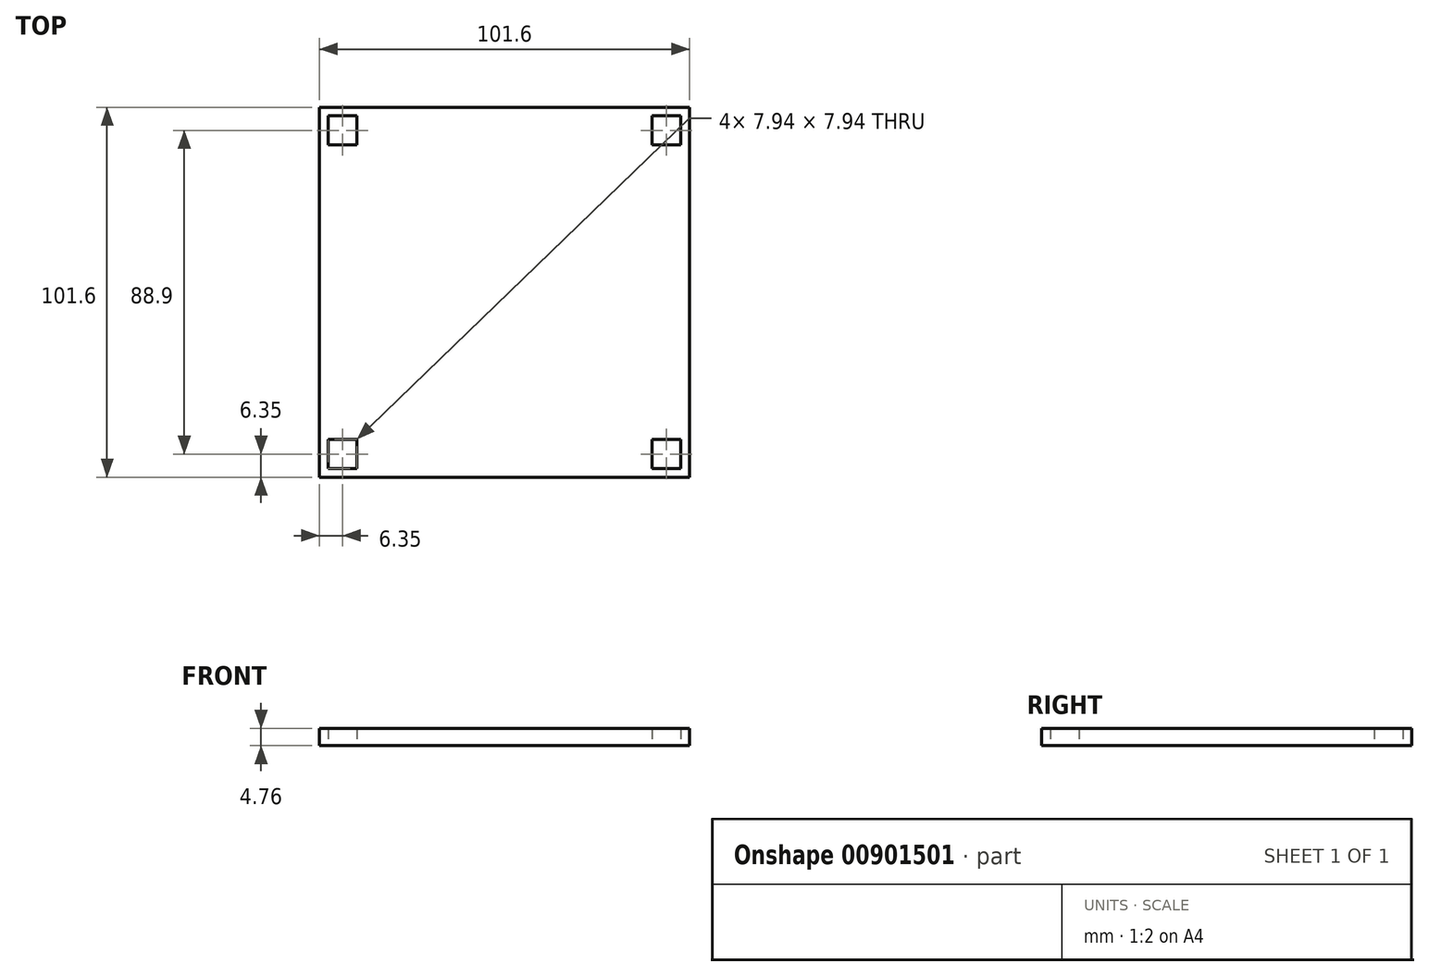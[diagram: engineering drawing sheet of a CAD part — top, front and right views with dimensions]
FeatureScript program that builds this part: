
annotation { "Feature Type Name" : "Feature", "Feature Type Description" : "" }
export const myFeature = defineFeature(function(context is Context, id is Id, definition is map)
    precondition{}
    {
        {
            var Q0;
            Q0=qCreatedBy(makeId("Top.planeOp"),FACE);
            var sketch = newSketch(context, id + "F0", { "sketchPlane" : qUnion([Q0])});
            skLineSegment(sketch, "E0.bottom", {"start": v(0, 0) * mm, "end": v(101.6, 0) * mm});
            skLineSegment(sketch, "E0.top", {"start": v(0, 101.6) * mm, "end": v(101.6, 101.6) * mm});
            skLineSegment(sketch, "E0.left", {"start": v(0, 0) * mm, "end": v(0, 101.6) * mm});
            skLineSegment(sketch, "E0.right", {"start": v(101.6, 0) * mm, "end": v(101.6, 101.6) * mm});
            skLineSegment(sketch, "E1.bottom", {"start": v(19.05, 12.7) * mm, "end": v(82.55, 12.7) * mm, "construction": true});
            skLineSegment(sketch, "E1.top", {"start": v(19.05, 88.9) * mm, "end": v(82.55, 88.9) * mm, "construction": true});
            skLineSegment(sketch, "E1.left", {"start": v(12.7, 19.05) * mm, "end": v(12.7, 82.55) * mm, "construction": true});
            skLineSegment(sketch, "E1.right", {"start": v(88.9, 19.05) * mm, "end": v(88.9, 82.55) * mm, "construction": true});
            skPoint(sketch, "E2.visualSharp", {"position": v(12.7, 12.7) * mm});
            skArc(sketch, "E2.filletArc", {"start": v(12.7, 19.05) * mm, "mid": v(14.56, 14.56) * mm, "end": v(19.05, 12.7) * mm, "construction": true});
            skPoint(sketch, "E3.visualSharp", {"position": v(88.9, 12.7) * mm});
            skArc(sketch, "E3.filletArc", {"start": v(82.55, 12.7) * mm, "mid": v(87.04, 14.56) * mm, "end": v(88.9, 19.05) * mm, "construction": true});
            skPoint(sketch, "E4.visualSharp", {"position": v(88.9, 88.9) * mm});
            skArc(sketch, "E4.filletArc", {"start": v(88.9, 82.55) * mm, "mid": v(87.04, 87.04) * mm, "end": v(82.55, 88.9) * mm, "construction": true});
            skPoint(sketch, "E5.visualSharp", {"position": v(12.7, 88.9) * mm});
            skArc(sketch, "E5.filletArc", {"start": v(19.05, 88.9) * mm, "mid": v(14.56, 87.04) * mm, "end": v(12.7, 82.55) * mm, "construction": true});
            skLineSegment(sketch, "E6", {"start": v(88.9, 12.7) * mm, "end": v(101.6, 0) * mm, "construction": true});
            skLineSegment(sketch, "E7", {"start": v(12.7, 12.7) * mm, "end": v(0, 0) * mm, "construction": true});
            skLineSegment(sketch, "E8", {"start": v(6.35, 6.35) * mm, "end": v(95.25, 6.35) * mm, "construction": true});
            skLineSegment(sketch, "E9", {"start": v(0, 101.6) * mm, "end": v(12.7, 88.9) * mm, "construction": true});
            skLineSegment(sketch, "E10", {"start": v(88.9, 88.9) * mm, "end": v(101.6, 101.6) * mm, "construction": true});
            skLineSegment(sketch, "E11", {"start": v(95.25, 95.25) * mm, "end": v(6.35, 95.25) * mm, "construction": true});
            skLineSegment(sketch, "E12", {"start": v(6.35, 95.25) * mm, "end": v(6.35, 6.35) * mm, "construction": true});
            skLineSegment(sketch, "E13", {"start": v(95.25, 6.35) * mm, "end": v(95.25, 95.25) * mm, "construction": true});
            skCircle(sketch, "E14", {"center": v(6.35, 95.25) * mm, "radius": 3.97 * mm, "construction": true});
            skCircle(sketch, "E15.0.1.0", {"center": v(6.35, 6.35) * mm, "radius": 3.97 * mm, "construction": true});
            skCircle(sketch, "E15.1.0.0", {"center": v(95.25, 95.25) * mm, "radius": 3.97 * mm, "construction": true});
            skCircle(sketch, "E15.1.1.0", {"center": v(95.25, 6.35) * mm, "radius": 3.97 * mm, "construction": true});
            skLineSegment(sketch, "E15.direction1", {"start": v(6.35, 95.25) * mm, "end": v(95.25, 95.25) * mm, "construction": true});
            skLineSegment(sketch, "E16.bottom", {"start": v(2.38, 2.38) * mm, "end": v(10.32, 2.38) * mm});
            skLineSegment(sketch, "E16.top", {"start": v(2.38, 10.32) * mm, "end": v(10.32, 10.32) * mm});
            skLineSegment(sketch, "E16.left", {"start": v(2.38, 2.38) * mm, "end": v(2.38, 10.32) * mm});
            skLineSegment(sketch, "E16.right", {"start": v(10.32, 2.38) * mm, "end": v(10.32, 10.32) * mm});
            skLineSegment(sketch, "E17.0.1.0", {"start": v(10.32, 91.28) * mm, "end": v(10.32, 99.22) * mm});
            skLineSegment(sketch, "E17.0.1.1", {"start": v(2.38, 99.22) * mm, "end": v(10.32, 99.22) * mm});
            skLineSegment(sketch, "E17.0.1.2", {"start": v(2.38, 91.28) * mm, "end": v(2.38, 99.22) * mm});
            skLineSegment(sketch, "E17.0.1.3", {"start": v(2.38, 91.28) * mm, "end": v(10.32, 91.28) * mm});
            skLineSegment(sketch, "E17.1.0.0", {"start": v(99.22, 2.38) * mm, "end": v(99.22, 10.32) * mm});
            skLineSegment(sketch, "E17.1.0.1", {"start": v(91.28, 10.32) * mm, "end": v(99.22, 10.32) * mm});
            skLineSegment(sketch, "E17.1.0.2", {"start": v(91.28, 2.38) * mm, "end": v(91.28, 10.32) * mm});
            skLineSegment(sketch, "E17.1.0.3", {"start": v(91.28, 2.38) * mm, "end": v(99.22, 2.38) * mm});
            skLineSegment(sketch, "E17.1.1.0", {"start": v(99.22, 91.28) * mm, "end": v(99.22, 99.22) * mm});
            skLineSegment(sketch, "E17.1.1.1", {"start": v(91.28, 99.22) * mm, "end": v(99.22, 99.22) * mm});
            skLineSegment(sketch, "E17.1.1.2", {"start": v(91.28, 91.28) * mm, "end": v(91.28, 99.22) * mm});
            skLineSegment(sketch, "E17.1.1.3", {"start": v(91.28, 91.28) * mm, "end": v(99.22, 91.28) * mm});
            skLineSegment(sketch, "E17.direction1", {"start": v(2.38, 2.38) * mm, "end": v(91.28, 2.38) * mm, "construction": true});
            skLineSegment(sketch, "E17.direction2", {"start": v(2.38, 2.38) * mm, "end": v(2.38, 91.28) * mm, "construction": true});
            skSolve(sketch);
        }
        {
            var Q0;
            Q0=makeQuery(id+"F0.imprint","IMPRINT",FACE,{"disambiguationData":[TD([[makeQuery(id+"F0.imprint","IMPRINT",EDGE,{"derivedFrom":sQuery(id+"F0.wireOp",EDGE,"E0.bottom")}),1.0]])]});
            extrude(context, id + "F1", {"entities" : qUnion([Q0]), "depth" : 4.76 * mm, "offsetDistance" : 25.4 * mm});
        }
    });
